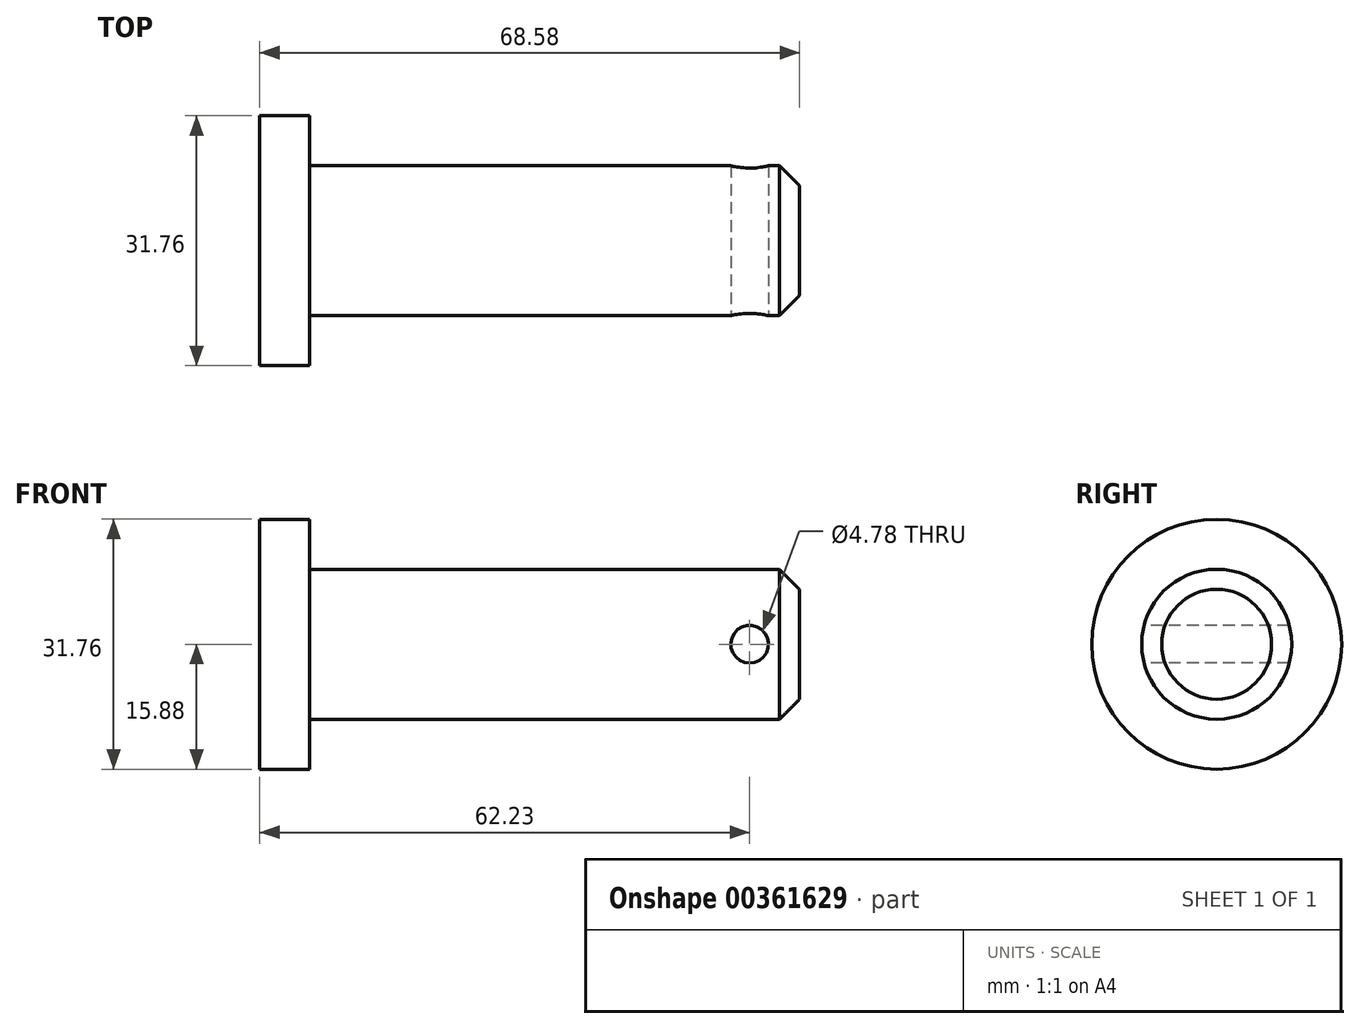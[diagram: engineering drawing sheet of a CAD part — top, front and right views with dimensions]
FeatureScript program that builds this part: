
annotation { "Feature Type Name" : "Feature", "Feature Type Description" : "" }
export const myFeature = defineFeature(function(context is Context, id is Id, definition is map)
    precondition{}
    {
        {
            var Q0;
            Q0=qCreatedBy(makeId("Right.planeOp"),FACE);
            var sketch = newSketch(context, id + "F0", { "sketchPlane" : qUnion([Q0])});
            skCircle(sketch, "E0", {"center": v(0, 0) * mm, "radius": 15.88 * mm});
            skSolve(sketch);
        }
        {
            var Q0;
            Q0 = qSketchRegion(id + "F0", true);
            extrude(context, id + "F1", {"entities" : qUnion([Q0]), "depth" : 6.35 * mm});
        }
        {
            var Q0;
            Q0=makeQuery(id+"F1.opExtrude","CAP_FACE",FACE,{"disambiguationData":[OSD([sQuery(id+"F0.wireOp",EDGE,"E0")])],"isStart":false});
            var sketch = newSketch(context, id + "F2", { "sketchPlane" : qUnion([Q0])});
            skCircle(sketch, "E1", {"center": v(0, 0) * mm, "radius": 9.52 * mm});
            skSolve(sketch);
        }
        {
            var Q0;
            Q0 = qSketchRegion(id + "F2", true);
            extrude(context, id + "F3", {"entities" : qUnion([Q0]), "operationType" : NewBodyOperationType.ADD, "depth" : 62.23 * mm});
        }
        {
            var Q0;
            Q0=makeQuery(id+"F3.opExtrude","CAP_EDGE",EDGE,{"disambiguationData":[OSD([sQuery(id+"F2.wireOp",EDGE,"E1")])],"isStart":false});
            chamfer(context, id + "F4", {"entities" : qUnion([Q0]), "width" : 2.54 * mm, "tangentPropagation" : true});
        }
        {
            var Q0;
            Q0=qCreatedBy(makeId("Front.planeOp"),FACE);
            var sketch = newSketch(context, id + "F5", { "sketchPlane" : qUnion([Q0])});
            skCircle(sketch, "E2", {"center": v(62.23, 0) * mm, "radius": 2.39 * mm});
            skSolve(sketch);
        }
        {
            var Q0;
            Q0 = qSketchRegion(id + "F5", true);
            extrude(context, id + "F6", {"entities" : qUnion([Q0]), "operationType" : NewBodyOperationType.REMOVE, "endBound" : BoundingType.THROUGH_ALL, "oppositeDirection" : true, "depth" : 25.4 * mm, "hasSecondDirection" : true, "secondDirectionOppositeDirection" : false, "secondDirectionDepth" : 25.4 * mm});
        }
    });
